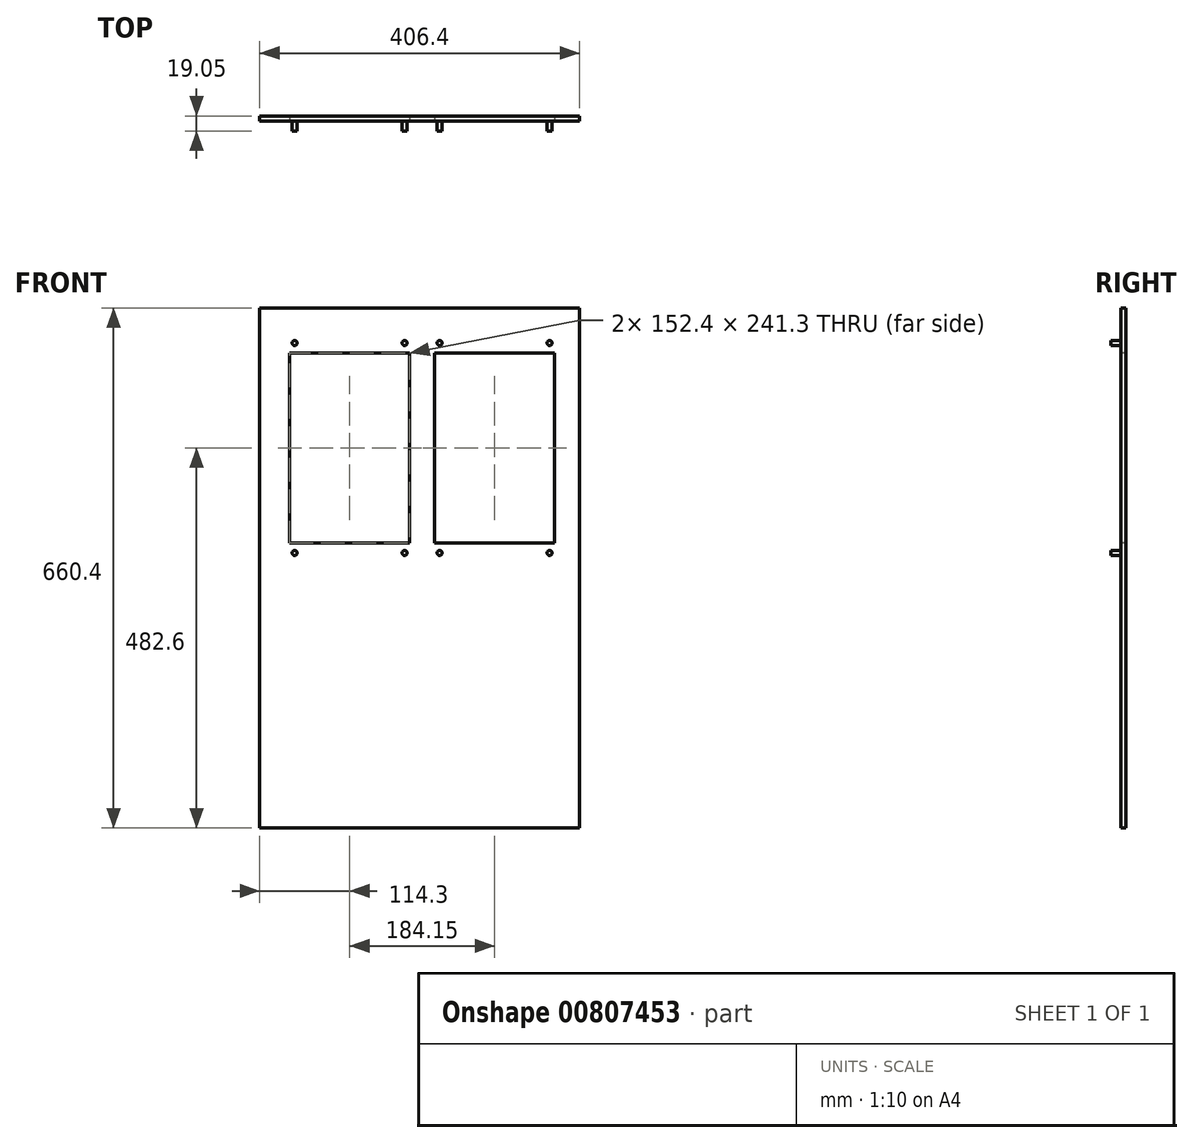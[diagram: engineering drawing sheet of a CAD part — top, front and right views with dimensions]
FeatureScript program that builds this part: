
annotation { "Feature Type Name" : "Feature", "Feature Type Description" : "" }
export const myFeature = defineFeature(function(context is Context, id is Id, definition is map)
    precondition{}
    {
        {
            var Q0;
            Q0=qCreatedBy(makeId("Front.planeOp"),FACE);
            var sketch = newSketch(context, id + "F0", { "sketchPlane" : qUnion([Q0])});
            skLineSegment(sketch, "E0.bottom", {"start": v(0, 0) * mm, "end": v(406.4, 0) * mm});
            skLineSegment(sketch, "E0.top", {"start": v(0, 660.4) * mm, "end": v(406.4, 660.4) * mm});
            skLineSegment(sketch, "E0.left", {"start": v(0, 0) * mm, "end": v(0, 660.4) * mm});
            skLineSegment(sketch, "E0.right", {"start": v(406.4, 0) * mm, "end": v(406.4, 660.4) * mm});
            skSolve(sketch);
        }
        {
            var Q0;
            Q0 = qSketchRegion(id + "F0", true);
            extrude(context, id + "F1", {"entities" : qUnion([Q0]), "depth" : 6.35 * mm, "offsetDistance" : 25.4 * mm});
        }
        {
            var Q0;
            Q0=makeQuery(id+"F1.opExtrude","CAP_FACE",FACE,{"disambiguationData":[OSD([sQuery(id+"F0.wireOp",EDGE,"E0.bottom"),sQuery(id+"F0.wireOp",EDGE,"E0.top"),sQuery(id+"F0.wireOp",EDGE,"E0.left"),sQuery(id+"F0.wireOp",EDGE,"E0.right")])],"isStart":false});
            var sketch = newSketch(context, id + "F2", { "sketchPlane" : qUnion([Q0])});
            skLineSegment(sketch, "E1.bottom", {"start": v(38.1, 603.25) * mm, "end": v(190.5, 603.25) * mm});
            skLineSegment(sketch, "E1.top", {"start": v(38.1, 361.95) * mm, "end": v(190.5, 361.95) * mm});
            skLineSegment(sketch, "E1.left", {"start": v(38.1, 603.25) * mm, "end": v(38.1, 361.95) * mm});
            skLineSegment(sketch, "E1.right", {"start": v(190.5, 603.25) * mm, "end": v(190.5, 361.95) * mm});
            skLineSegment(sketch, "E2.bottom", {"start": v(222.25, 603.25) * mm, "end": v(374.65, 603.25) * mm});
            skLineSegment(sketch, "E2.top", {"start": v(222.25, 361.95) * mm, "end": v(374.65, 361.95) * mm});
            skLineSegment(sketch, "E2.left", {"start": v(222.25, 603.25) * mm, "end": v(222.25, 361.95) * mm});
            skLineSegment(sketch, "E2.right", {"start": v(374.65, 603.25) * mm, "end": v(374.65, 361.95) * mm});
            skSolve(sketch);
        }
        {
            var Q0;
            Q0=makeQuery(id+"F2.imprint","IMPRINT",FACE,{"disambiguationData":[TD([[makeQuery(id+"F2.imprint","IMPRINT",EDGE,{"derivedFrom":sQuery(id+"F2.wireOp",EDGE,"E1.bottom")}),-1.0]])]});
            var Q1;
            Q1=makeQuery(id+"F2.imprint","IMPRINT",FACE,{"disambiguationData":[TD([[makeQuery(id+"F2.imprint","IMPRINT",EDGE,{"derivedFrom":sQuery(id+"F2.wireOp",EDGE,"E2.bottom")}),-1.0]])]});
            extrude(context, id + "F3", {"entities" : qUnion([Q0, Q1]), "operationType" : NewBodyOperationType.REMOVE, "endBound" : BoundingType.THROUGH_ALL, "oppositeDirection" : true, "depth" : 25.4 * mm, "offsetDistance" : 25.4 * mm});
        }
        {
            var Q0;
            Q0=makeQuery(id+"F1.opExtrude","CAP_FACE",FACE,{"disambiguationData":[OSD([sQuery(id+"F0.wireOp",EDGE,"E0.bottom"),sQuery(id+"F0.wireOp",EDGE,"E0.top"),sQuery(id+"F0.wireOp",EDGE,"E0.left"),sQuery(id+"F0.wireOp",EDGE,"E0.right")])],"isStart":false});
            var sketch = newSketch(context, id + "F4", { "sketchPlane" : qUnion([Q0])});
            skPoint(sketch, "E3", {"position": v(44.45, 615.95) * mm});
            skLineSegment(sketch, "E4", {"start": v(114.3, 603.25) * mm, "end": v(114.3, 361.95) * mm});
            skLineSegment(sketch, "E5", {"start": v(38.1, 482.6) * mm, "end": v(190.5, 482.6) * mm});
            skLineSegment(sketch, "E6", {"start": v(298.45, 603.25) * mm, "end": v(298.45, 361.95) * mm});
            skLineSegment(sketch, "E7", {"start": v(222.25, 482.6) * mm, "end": v(374.65, 482.6) * mm});
            skPoint(sketch, "E8.MirrorP", {"position": v(44.45, 349.25) * mm});
            skLineSegment(sketch, "E9.MirrorCS", {"start": v(114.3, 361.95) * mm, "end": v(114.3, 603.25) * mm});
            skPoint(sketch, "E10.MirrorP", {"position": v(184.15, 615.95) * mm});
            skPoint(sketch, "E11.MirrorP", {"position": v(184.15, 349.25) * mm});
            skCircle(sketch, "E12", {"center": v(44.45, 615.95) * mm, "radius": 3.18 * mm});
            skCircle(sketch, "E13", {"center": v(184.15, 615.95) * mm, "radius": 3.18 * mm});
            skCircle(sketch, "E14", {"center": v(44.45, 349.25) * mm, "radius": 3.17 * mm});
            skCircle(sketch, "E15", {"center": v(184.15, 349.25) * mm, "radius": 3.18 * mm});
            skPoint(sketch, "E16", {"position": v(228.6, 615.95) * mm});
            skPoint(sketch, "E17.MirrorP", {"position": v(368.3, 615.95) * mm});
            skPoint(sketch, "E18.MirrorP", {"position": v(228.6, 349.25) * mm});
            skPoint(sketch, "E19.MirrorP", {"position": v(368.3, 349.25) * mm});
            skCircle(sketch, "E20", {"center": v(228.6, 615.95) * mm, "radius": 3.18 * mm});
            skCircle(sketch, "E21", {"center": v(368.3, 615.95) * mm, "radius": 3.18 * mm});
            skCircle(sketch, "E22", {"center": v(228.6, 349.25) * mm, "radius": 3.18 * mm});
            skCircle(sketch, "E23", {"center": v(368.3, 349.25) * mm, "radius": 3.18 * mm});
            skSolve(sketch);
        }
        {
            var Q0;
            Q0=makeQuery(id+"F4.imprint","IMPRINT",FACE,{"disambiguationData":[TD([[makeQuery(id+"F4.imprint","IMPRINT",EDGE,{"derivedFrom":sQuery(id+"F4.wireOp",EDGE,"E12")}),1.0]])]});
            var Q1;
            Q1=makeQuery(id+"F4.imprint","IMPRINT",FACE,{"disambiguationData":[TD([[makeQuery(id+"F4.imprint","IMPRINT",EDGE,{"derivedFrom":sQuery(id+"F4.wireOp",EDGE,"E13")}),1.0]])]});
            var Q2;
            Q2=makeQuery(id+"F4.imprint","IMPRINT",FACE,{"disambiguationData":[TD([[makeQuery(id+"F4.imprint","IMPRINT",EDGE,{"derivedFrom":sQuery(id+"F4.wireOp",EDGE,"E14")}),1.0]])]});
            var Q3;
            Q3=makeQuery(id+"F4.imprint","IMPRINT",FACE,{"disambiguationData":[TD([[makeQuery(id+"F4.imprint","IMPRINT",EDGE,{"derivedFrom":sQuery(id+"F4.wireOp",EDGE,"E15")}),1.0]])]});
            var Q4;
            Q4=makeQuery(id+"F4.imprint","IMPRINT",FACE,{"disambiguationData":[TD([[makeQuery(id+"F4.imprint","IMPRINT",EDGE,{"derivedFrom":sQuery(id+"F4.wireOp",EDGE,"E20")}),1.0]])]});
            var Q5;
            Q5=makeQuery(id+"F4.imprint","IMPRINT",FACE,{"disambiguationData":[TD([[makeQuery(id+"F4.imprint","IMPRINT",EDGE,{"derivedFrom":sQuery(id+"F4.wireOp",EDGE,"E21")}),1.0]])]});
            var Q6;
            Q6=makeQuery(id+"F4.imprint","IMPRINT",FACE,{"disambiguationData":[TD([[makeQuery(id+"F4.imprint","IMPRINT",EDGE,{"derivedFrom":sQuery(id+"F4.wireOp",EDGE,"E22")}),1.0]])]});
            var Q7;
            Q7=makeQuery(id+"F4.imprint","IMPRINT",FACE,{"disambiguationData":[TD([[makeQuery(id+"F4.imprint","IMPRINT",EDGE,{"derivedFrom":sQuery(id+"F4.wireOp",EDGE,"E23")}),1.0]])]});
            extrude(context, id + "F5", {"entities" : qUnion([Q0, Q1, Q2, Q3, Q4, Q5, Q6, Q7]), "operationType" : NewBodyOperationType.ADD, "depth" : 12.7 * mm, "offsetDistance" : 25.4 * mm});
        }
    });
